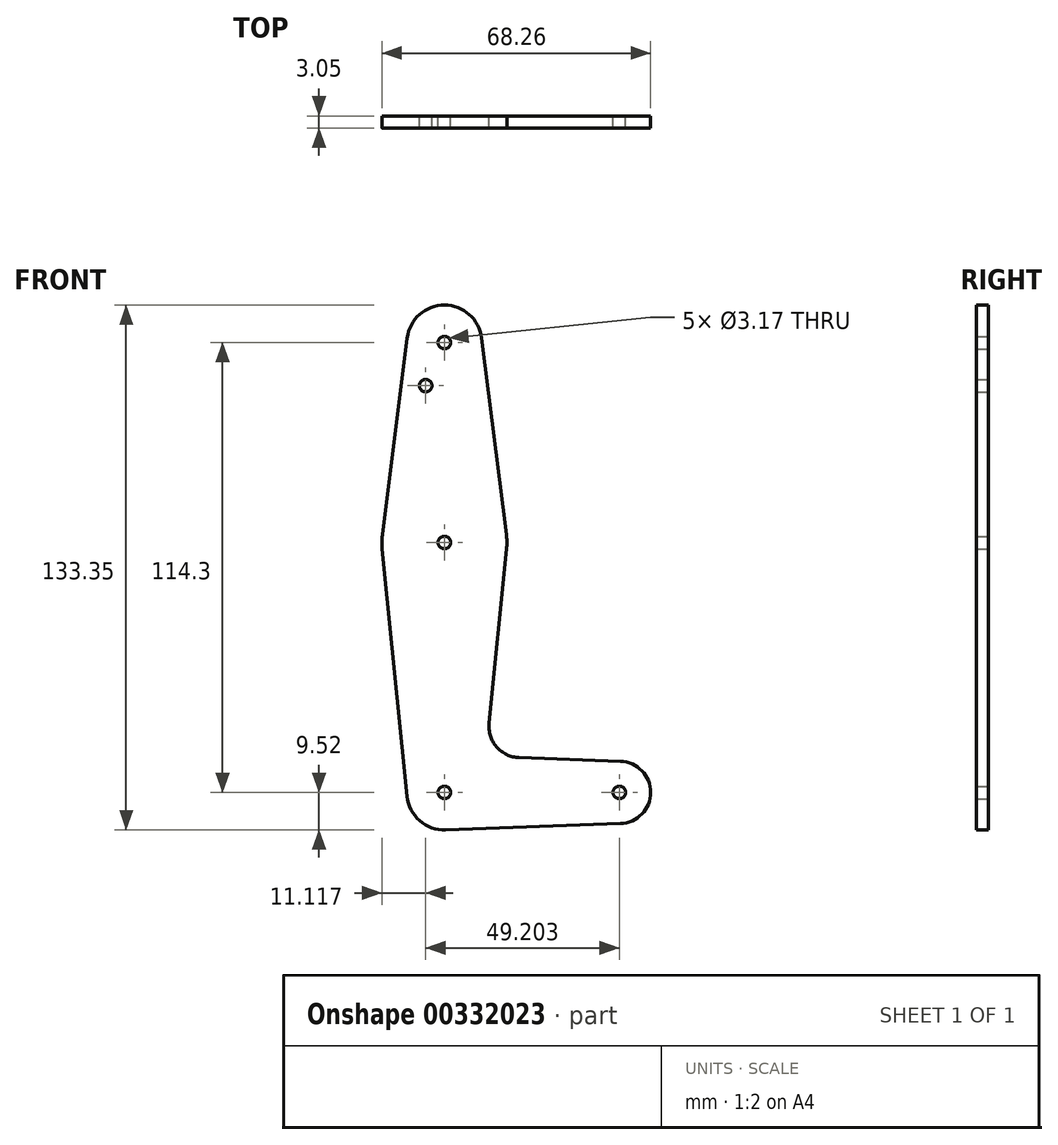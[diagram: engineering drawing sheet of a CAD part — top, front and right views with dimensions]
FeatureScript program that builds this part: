
annotation { "Feature Type Name" : "Feature", "Feature Type Description" : "" }
export const myFeature = defineFeature(function(context is Context, id is Id, definition is map)
    precondition{}
    {
        {
            var Q0;
            Q0=qCreatedBy(makeId("Front.planeOp"),FACE);
            var sketch = newSketch(context, id + "F0", { "sketchPlane" : qUnion([Q0])});
            skLineSegment(sketch, "E0", {"start": v(0, 0) * mm, "end": v(0, 114.3) * mm, "construction": true});
            skLineSegment(sketch, "E1", {"start": v(0, 0) * mm, "end": v(44.45, 0) * mm, "construction": true});
            skCircle(sketch, "E2", {"center": v(0, 63.5) * mm, "radius": 15.88 * mm});
            skCircle(sketch, "E3", {"center": v(44.45, 0) * mm, "radius": 7.94 * mm});
            skCircle(sketch, "E4", {"center": v(0, 114.3) * mm, "radius": 9.53 * mm});
            skCircle(sketch, "E5", {"center": v(0, 0) * mm, "radius": 9.53 * mm});
            skLineSegment(sketch, "E6", {"start": v(-9.45, 115.5) * mm, "end": v(-15.75, 65.48) * mm});
            skLineSegment(sketch, "E7", {"start": v(9.45, 115.5) * mm, "end": v(15.75, 65.48) * mm});
            skLineSegment(sketch, "E8", {"start": v(-15.8, 61.91) * mm, "end": v(-9.48, -0.95) * mm});
            skLineSegment(sketch, "E9", {"start": v(15.8, 61.91) * mm, "end": v(11.34, 17.6) * mm});
            skLineSegment(sketch, "E10", {"start": v(18.97, 8.85) * mm, "end": v(44.73, 7.93) * mm});
            skLineSegment(sketch, "E11", {"start": v(0.34, -9.52) * mm, "end": v(44.73, -7.93) * mm});
            skCircle(sketch, "E12", {"center": v(0, 114.3) * mm, "radius": 1.59 * mm});
            skCircle(sketch, "E13", {"center": v(0, 63.5) * mm, "radius": 1.59 * mm});
            skCircle(sketch, "E14", {"center": v(0, 0) * mm, "radius": 1.59 * mm});
            skCircle(sketch, "E15", {"center": v(44.45, 0) * mm, "radius": 1.59 * mm});
            skCircle(sketch, "E16", {"center": v(-4.75, 103.35) * mm, "radius": 1.59 * mm});
            skArc(sketch, "E17.filletArc", {"start": v(11.34, 17.6) * mm, "mid": v(13.26, 11.57) * mm, "end": v(18.97, 8.85) * mm});
            skSolve(sketch);
        }
        {
            var Q0;
            Q0 = qSketchRegion(id + "F0", true);
            extrude(context, id + "F1", {"entities" : qUnion([Q0]), "depth" : 3.05 * mm});
        }
    });
